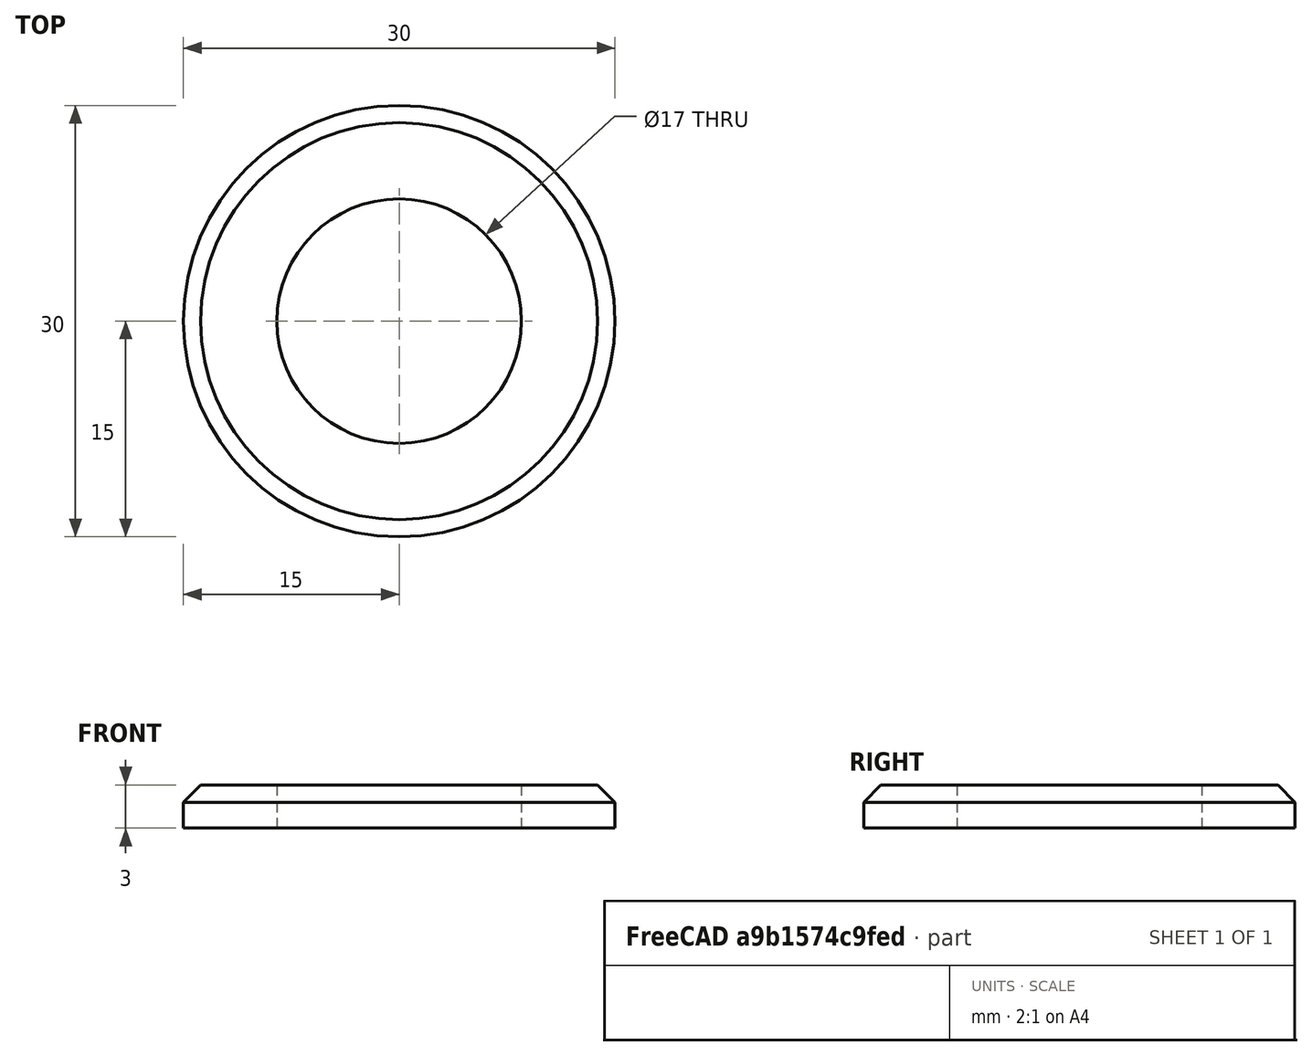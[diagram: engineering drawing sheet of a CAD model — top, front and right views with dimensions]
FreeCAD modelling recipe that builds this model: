
FCSTD DOCUMENT  (FreeCAD 0.15R4651 (Git))
Label: Scheibe_DIN125-B 17
License: CC-BY 3.0
LicenseURL: http://creativecommons.org/licenses/by/3.0/
objects: Sketcher::SketchObject×1, PartDesign::Revolution×1
note: 3 computed .brp shape members not serialized (recipe doc carries the construction recipe); baked Part::Feature solids carry a one-line shape summary decoded from their .brp

FEATURE [Sketcher::SketchObject] Sketch
  Placement = pos=(0,0,0) rot=(0.57735,0.57735,0.57735;2.0944rad)
  sketch-geometry (5):
    g0: LineSegment StartX=8.5 StartY=0 StartZ=0 EndX=15 EndY=0 EndZ=0
    g1: LineSegment StartX=15 StartY=0 StartZ=0 EndX=15 EndY=1.8 EndZ=0
    g2: LineSegment StartX=13.8 StartY=3 StartZ=0 EndX=8.5 EndY=3 EndZ=0
    g3: LineSegment StartX=8.5 StartY=3 StartZ=0 EndX=8.5 EndY=0 EndZ=0
    g4: LineSegment StartX=13.8 StartY=3 StartZ=0 EndX=15 EndY=1.8 EndZ=0
  constraints (15):
    c: Coincident(g0,g1)
    c: Coincident(g2,g3)
    c: Coincident(g3,g0)
    c: Horizontal(g0)
    c: Horizontal(g2)
    c: Vertical(g1)
    c: Vertical(g3)
    c: PointOnObject(g0,g-1)
    c: DistanceX(g-1,g2) = 8.5
    c: Coincident(g1,g4)
    c: Coincident(g2,g4)
    c: DistanceY(g3) = -3
    c: DistanceX(g-1,g1) = 15
    c: DistanceX(g4) = 1.2
    c: DistanceY(g4) = -1.2
FEATURE [PartDesign::Revolution] Revolution  label="Scheibe DIN 125 - B 17 #"
  Angle = 360
  Axis = (0,0,1)
  Base = (0,0,0)
  Placement = pos=(0,0,0) rot=(0.57735,0.57735,0.57735;2.0944rad)
  ReferenceAxis = -> Sketch [V_Axis]
  Reversed = true
  Sketch = -> Sketch
